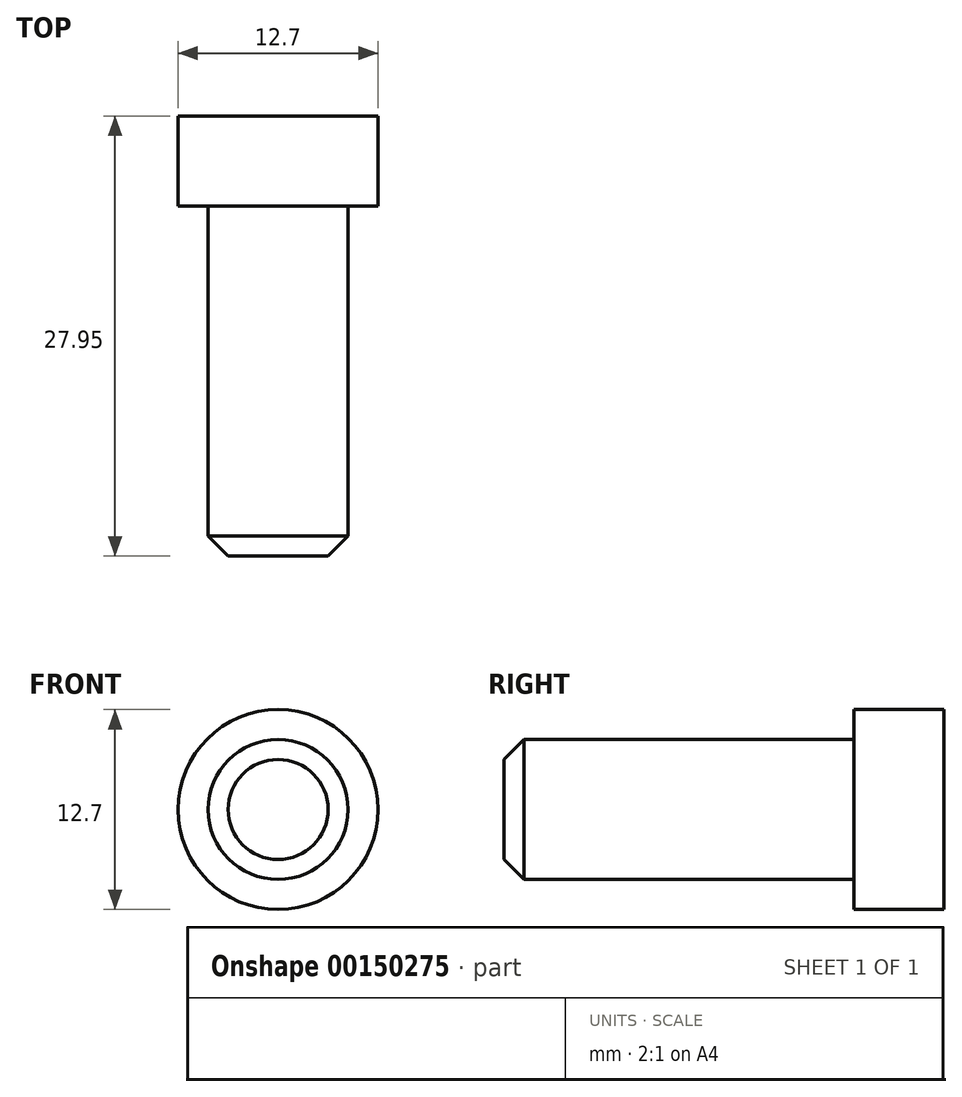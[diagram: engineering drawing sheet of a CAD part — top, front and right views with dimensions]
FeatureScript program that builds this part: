
annotation { "Feature Type Name" : "Feature", "Feature Type Description" : "" }
export const myFeature = defineFeature(function(context is Context, id is Id, definition is map)
    precondition{}
    {
        {
            var Q0;
            Q0=qCreatedBy(makeId("Front.planeOp"),FACE);
            var sketch = newSketch(context, id + "F0", { "sketchPlane" : qUnion([Q0])});
            skCircle(sketch, "E0", {"center": v(0, 0) * mm, "radius": 4.45 * mm});
            skSolve(sketch);
        }
        {
            var Q0;
            Q0 = qSketchRegion(id + "F0", true);
            extrude(context, id + "F1", {"entities" : qUnion([Q0]), "depth" : 22.22 * mm});
        }
        {
            var Q0;
            Q0=makeQuery(id+"F1.opExtrude","CAP_FACE",FACE,{"disambiguationData":[OSD([sQuery(id+"F0.wireOp",EDGE,"E0")])],"isStart":true});
            var sketch = newSketch(context, id + "F2", { "sketchPlane" : qUnion([Q0])});
            skCircle(sketch, "E1", {"center": v(0, 0) * mm, "radius": 6.35 * mm});
            skSolve(sketch);
        }
        {
            var Q0;
            Q0=makeQuery(id+"F2.imprint","IMPRINT",FACE,{"disambiguationData":[TD([[makeQuery(id+"F2.imprint","IMPRINT",EDGE,{"derivedFrom":makeQuery(id+"F1.opExtrude","CAP_EDGE",EDGE,{"disambiguationData":[OSD([sQuery(id+"F0.wireOp",EDGE,"E0")])],"isStart":true})}),-1.0]])]});
            var Q1;
            Q1=makeQuery(id+"F2.imprint","IMPRINT",FACE,{"disambiguationData":[TD([[makeQuery(id+"F2.imprint","IMPRINT",EDGE,{"derivedFrom":sQuery(id+"F2.wireOp",EDGE,"E1")}),1.0]])]});
            extrude(context, id + "F3", {"entities" : qUnion([Q0, Q1]), "operationType" : NewBodyOperationType.ADD, "depth" : 5.7 * mm});
        }
        {
            var Q0;
            Q0=makeQuery(id+"F1.opExtrude","CAP_EDGE",EDGE,{"disambiguationData":[OSD([sQuery(id+"F0.wireOp",EDGE,"E0")])],"isStart":false});
            chamfer(context, id + "F4", {"entities" : qUnion([Q0]), "width" : 1.27 * mm, "tangentPropagation" : true});
        }
    });
